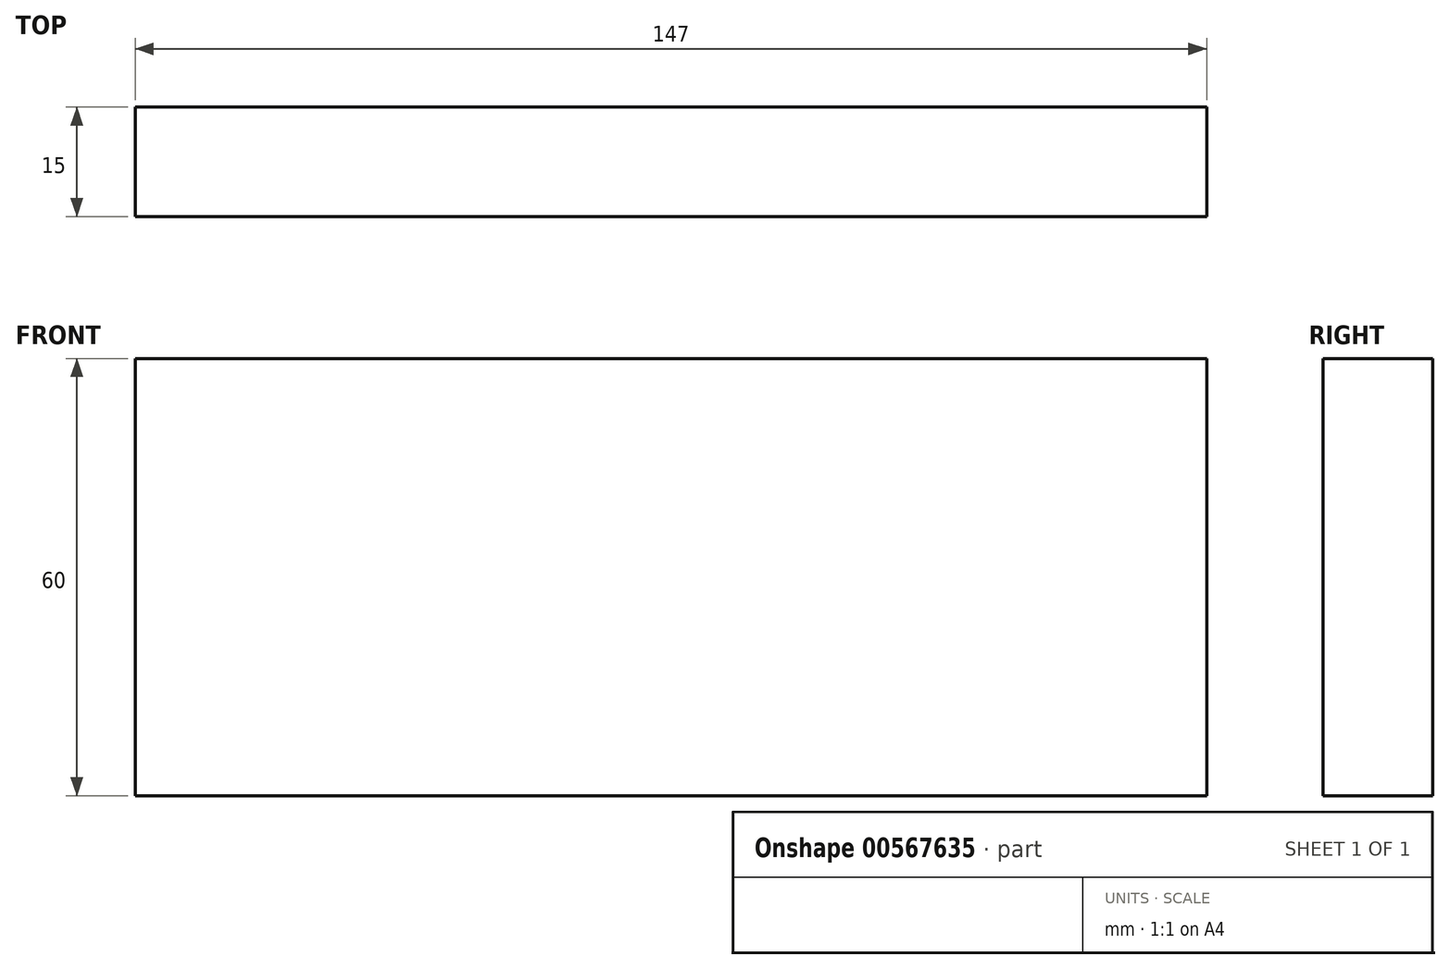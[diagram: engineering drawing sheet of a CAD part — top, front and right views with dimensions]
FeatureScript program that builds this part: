
annotation { "Feature Type Name" : "Feature", "Feature Type Description" : "" }
export const myFeature = defineFeature(function(context is Context, id is Id, definition is map)
    precondition{}
    {
        {
            var Q0;
            Q0=qCreatedBy(makeId("Right.planeOp"),FACE);
            var sketch = newSketch(context, id + "F0", { "sketchPlane" : qUnion([Q0])});
            skLineSegment(sketch, "E0.bottom", {"start": v(7.5, -30) * mm, "end": v(-7.5, -30) * mm});
            skLineSegment(sketch, "E0.top", {"start": v(7.5, 30) * mm, "end": v(-7.5, 30) * mm});
            skLineSegment(sketch, "E0.left", {"start": v(7.5, -30) * mm, "end": v(7.5, 30) * mm});
            skLineSegment(sketch, "E0.right", {"start": v(-7.5, -30) * mm, "end": v(-7.5, 30) * mm});
            skPoint(sketch, "E0.middle", {"position": v(0, 0) * mm});
            skSolve(sketch);
        }
        {
            var Q0;
            Q0 = qSketchRegion(id + "F0", true);
            extrude(context, id + "F1", {"entities" : qUnion([Q0]), "depth" : 147 * mm, "offsetDistance" : 25 * mm});
        }
    });
